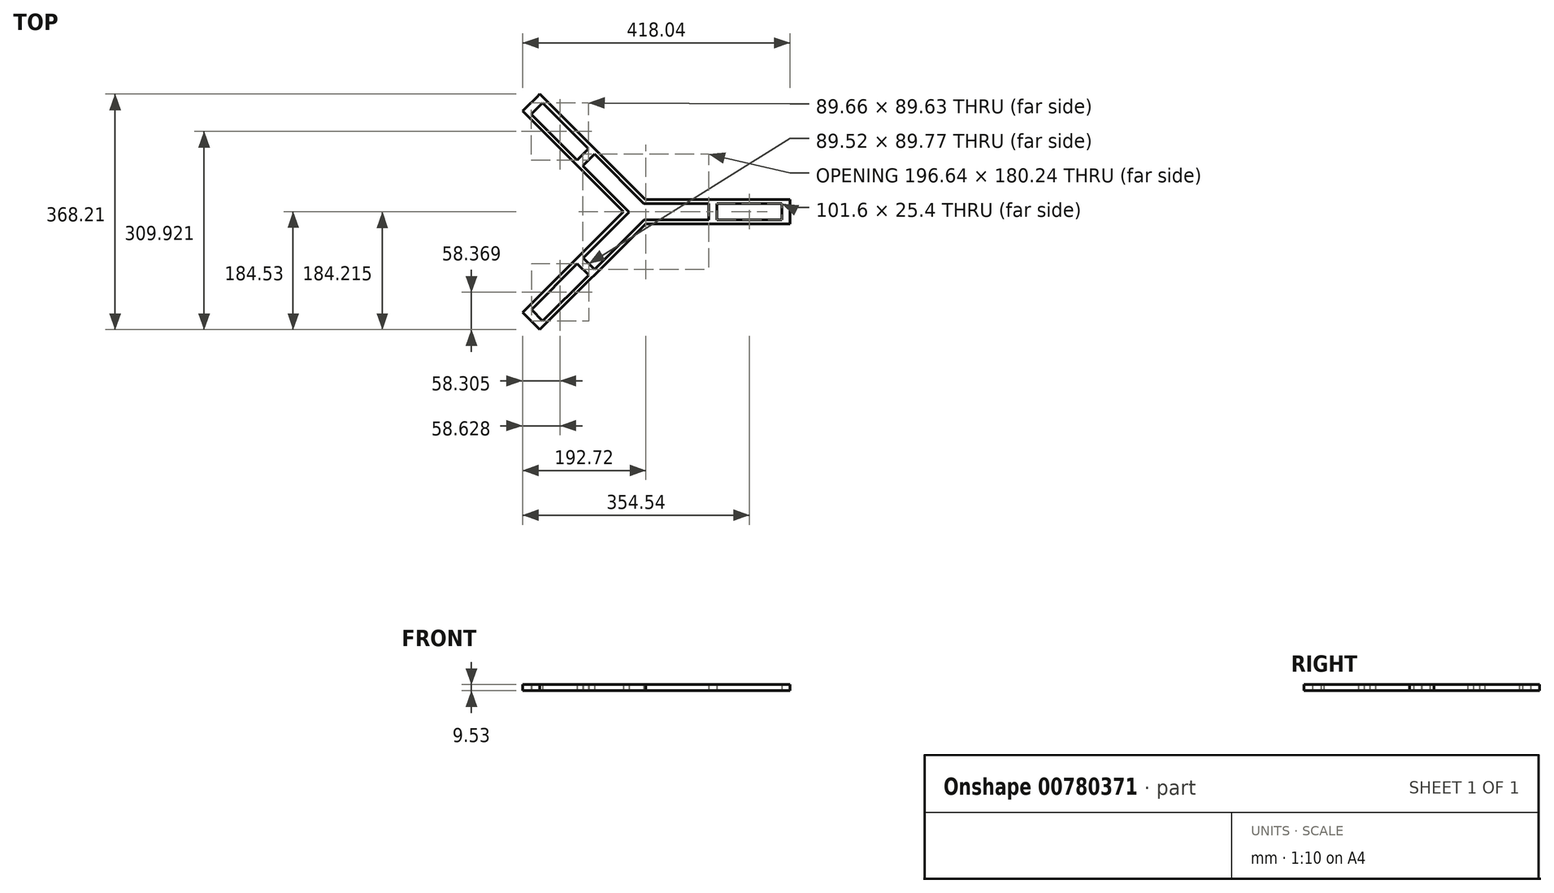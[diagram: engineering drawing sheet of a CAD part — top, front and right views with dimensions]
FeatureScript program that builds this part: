
annotation { "Feature Type Name" : "Feature", "Feature Type Description" : "" }
export const myFeature = defineFeature(function(context is Context, id is Id, definition is map)
    precondition{}
    {
        {
            var Q0;
            Q0=qCreatedBy(makeId("Top.planeOp"),FACE);
            var sketch = newSketch(context, id + "F0", { "sketchPlane" : qUnion([Q0])});
            skLineSegment(sketch, "E0", {"start": v(-85.16, -72.5) * mm, "end": v(-67.18, -90.43) * mm});
            skLineSegment(sketch, "E1.0", {"start": v(-94.34, -81.28) * mm, "end": v(-76.36, -99.21) * mm});
            skLineSegment(sketch, "E2", {"start": v(-503.14, -0.88) * mm, "end": v(563.66, 0.5) * mm, "construction": true});
            skLineSegment(sketch, "E3.MirrorCS", {"start": v(-94.55, 80.58) * mm, "end": v(-76.62, 98.56) * mm});
            skLineSegment(sketch, "E4.MirrorCS", {"start": v(-85.35, 71.82) * mm, "end": v(-67.41, 89.8) * mm});
            skLineSegment(sketch, "E5", {"start": v(111.3, 12.7) * mm, "end": v(111.3, -12.7) * mm});
            skLineSegment(sketch, "E6.0", {"start": v(124, 12.7) * mm, "end": v(124, -12.7) * mm});
            skLineSegment(sketch, "E7", {"start": v(-166.28, 152.54) * mm, "end": v(-148.65, 170.2) * mm});
            skLineSegment(sketch, "E8.0", {"start": v(-175.27, 161.5) * mm, "end": v(-157.65, 179.17) * mm});
            skLineSegment(sketch, "E9.MirrorCS", {"start": v(-165.88, -153.42) * mm, "end": v(-148.21, -171.04) * mm});
            skLineSegment(sketch, "E10.MirrorCS", {"start": v(-174.85, -162.41) * mm, "end": v(-157.18, -180.04) * mm});
            skLineSegment(sketch, "E11", {"start": v(225.6, 12.7) * mm, "end": v(225.6, -12.7) * mm});
            skLineSegment(sketch, "E12", {"start": v(-175.27, 161.5) * mm, "end": v(-179.75, 157.01) * mm});
            skLineSegment(sketch, "E13", {"start": v(-179.75, 157.01) * mm, "end": v(-22.08, -0.26) * mm});
            skLineSegment(sketch, "E14", {"start": v(-174.85, -162.41) * mm, "end": v(-179.35, -157.93) * mm});
            skLineSegment(sketch, "E15", {"start": v(-179.35, -157.93) * mm, "end": v(-22.08, -0.26) * mm});
            skLineSegment(sketch, "E16", {"start": v(-157.65, 179.17) * mm, "end": v(-153.17, 183.68) * mm});
            skLineSegment(sketch, "E17", {"start": v(-153.17, 183.68) * mm, "end": v(12.3, 19.05) * mm});
            skLineSegment(sketch, "E18", {"start": v(-166.28, 152.54) * mm, "end": v(-94.55, 80.58) * mm});
            skLineSegment(sketch, "E19", {"start": v(-85.35, 71.82) * mm, "end": v(-13.1, -0.88) * mm});
            skLineSegment(sketch, "E20", {"start": v(-85.16, -72.5) * mm, "end": v(-13.1, -0.88) * mm});
            skLineSegment(sketch, "E21", {"start": v(-94.34, -81.28) * mm, "end": v(-165.88, -153.42) * mm});
            skLineSegment(sketch, "E22", {"start": v(-67.41, 89.8) * mm, "end": v(9.7, 12.7) * mm});
            skLineSegment(sketch, "E23", {"start": v(-148.65, 170.2) * mm, "end": v(-76.62, 98.56) * mm});
            skLineSegment(sketch, "E24", {"start": v(9.7, 12.7) * mm, "end": v(111.3, 12.7) * mm});
            skLineSegment(sketch, "E25", {"start": v(124, 12.7) * mm, "end": v(225.6, 12.7) * mm});
            skLineSegment(sketch, "E26", {"start": v(225.6, -12.7) * mm, "end": v(124, -12.7) * mm});
            skLineSegment(sketch, "E27", {"start": v(111.3, -12.7) * mm, "end": v(10.55, -12.7) * mm});
            skLineSegment(sketch, "E28", {"start": v(-67.18, -90.43) * mm, "end": v(10.55, -12.7) * mm});
            skLineSegment(sketch, "E29", {"start": v(-76.36, -99.21) * mm, "end": v(-148.21, -171.04) * mm});
            skLineSegment(sketch, "E30", {"start": v(-174.85, -162.41) * mm, "end": v(-165.88, -153.42) * mm, "construction": true});
            skLineSegment(sketch, "E31", {"start": v(238.3, 12.7) * mm, "end": v(238.3, 19.05) * mm});
            skLineSegment(sketch, "E32", {"start": v(238.3, -12.7) * mm, "end": v(238.3, -19.05) * mm});
            skLineSegment(sketch, "E33.MirrorCS", {"start": v(-152.7, -184.53) * mm, "end": v(12.78, -19.05) * mm});
            skLineSegment(sketch, "E34.MirrorCS", {"start": v(-157.18, -180.04) * mm, "end": v(-152.7, -184.53) * mm});
            skPoint(sketch, "E35.trimOffspring.end.orphan", {"position": v(24.01, -7.82) * mm});
            skPoint(sketch, "E36.orphan", {"position": v(24, 7.43) * mm});
            skLineSegment(sketch, "E37", {"start": v(225.6, -12.7) * mm, "end": v(238.3, -12.7) * mm, "construction": true});
            skLineSegment(sketch, "E38", {"start": v(238.3, 12.7) * mm, "end": v(225.6, 12.7) * mm, "construction": true});
            skLineSegment(sketch, "E39", {"start": v(238.3, 19.05) * mm, "end": v(12.3, 19.05) * mm});
            skLineSegment(sketch, "E40", {"start": v(238.3, -19.05) * mm, "end": v(12.78, -19.05) * mm});
            skLineSegment(sketch, "E41", {"start": v(238.3, 12.7) * mm, "end": v(238.3, -12.7) * mm});
            skSolve(sketch);
        }
        {
            var Q0;
            Q0=makeQuery(id+"F0.imprint","IMPRINT",FACE,{"disambiguationData":[TD([[makeQuery(id+"F0.imprint","IMPRINT",EDGE,{"derivedFrom":sQuery(id+"F0.wireOp",EDGE,"E0")}),-1.0]])]});
            extrude(context, id + "F1", {"entities" : qUnion([Q0]), "depth" : 9.52 * mm, "offsetDistance" : 25.4 * mm});
        }
    });
